# Revit family: IS_ConceptAir_Multiproduct_BIM_GB_E0848;E0849;E0851;E0852
name_source: partatom
category: Plumbing Fixtures
revit_build: Autodesk Revit MEP 2014 (Build: 20140709_2115(x64)
units: mm (PartAtom-declared; Revit-internal decimal feet)

## types (24) — shared parameters
Accessories = www.idealspec.co.uk
AreaUnits = millimeters
Assembly Code = C1030200
AssetType = Fixed
BREEAM = No
Brand = Ideal Standard
Default Elevation = 800 mm  [stored 2.62467 ft]
DurationUnit = year
ECA = No
ExpectedLife = 10
Finish = White
IfcExportAs = IfcFurnitureType
IfcExportType = USERDEFINED
InstallationInstructions = www.idealspec.co.uk/resources.html
LinearUnits = millimeters
MainColor = White
ManufacturerURL = www.idealspec.co.uk
Material = Laquered MDF
NBSDescription = Bathroom integrated duct work
NBSReference = 45-35-72/320
NettWeight = 0 Kg
NominalDepth = 440 mm  [stored 1.44357 ft]
NominalHeight = 18 mm  [stored 0.0590551 ft]
NominalLength = 440 mm  [stored 1.44357 ft]
Shape = Rectangular
Space = Internal
SpareParts = www.fastpart-spares.co.uk
TMV3 = No
URL = www.idealspec.co.uk
Uniclass2 = Pr_40_30_78_04
Version = 1
VolumeUnits = Litres
WRAS = No
WarrantyDescription = Manufacturers warranty
WarrantyDurationParts = 5
WarrantyDurationUnit = year
WaterEfficientProduct = No
zero-valued in all types: CWFU, Cost, HWFU, WFU

## per-type parameters (varying)
| type | BIMObjectName | Color | Description | Features | MainColour | Model | ModelNumber | ModelReference | Name | NominalWidth | ProductInformation | Size |
| E0852VY - 120CM Worktop for Vessel Installation Matt Dark Brown | ISI_IdealStandard_Furniture_ConceptAir_E0852VY | Dark brown | Concept Air 120 cm Worktop For Vessel Installation Matt Dark Brown | 120 cm Worktop For Vessel Installation Matt Dark Brown | ISI_IdealStandard_Furniture_DarkBrown_Render | E0852VY | E0852VY | 120CM Worktop for Vessel Installation Gls Dark Brown + Matt White | Furniture_ConceptAir_E0852VY_IdealStandard | 1200 mm | www.idealspec.co.uk/assets/datasheet/E0852VY | 442 x 18 x 1204 mm |
| E0852UK - 120CM Worktop for Vessel Installation Wood Light Brown | ISI_IdealStandard_Furniture_ConceptAir_E0852UK | Wood brown | Concept Air 120 cm Worktop For Vessel Installation Wood Light Brown | 120 cm Worktop For Vessel Installation Wood Light Brown | ISI_IdealStandard_Furniture_WoodLightBrown_Render | E0852UK | E0852UK | 120CM Worktop for Vessel Installation Wood Light Brown + Matt Light Brown | Furniture_ConceptAir_E0852UK_IdealStandard | 1200 mm | www.idealspec.co.uk/assets/datasheet/E0852UK | 442 x 18 x 1204 mm |
| E0852PS - 120CM Worktop for Vessel Installation Wood Light Grey | ISI_IdealStandard_Furniture_ConceptAir_E0852PS | Wood grey | Concept Air 120 cm Worktop For Vessel Installation Wood Light Grey | 120 cm Worktop For Vessel Installation Wood Light Grey | ISI_IdealStandard_Furniture_WoodLightGrey_Render | E0852PS | E0852PS | 120CM Worktop for Vessel Installation Wood Light Grey + Matt White | Furniture_ConceptAir_E0852PS_IdealStandard | 1200 mm | www.idealspec.co.uk/assets/datasheet/E0852PS | 442 x 18 x 1204 mm |
| E0852KN - 120CM Worktop for Vessel Installation Gls White | ISI_IdealStandard_Furniture_ConceptAir_E0852KN | White | Concept Air 120 cm Worktop For Vessel Installation Gls White | 120 cm Worktop For Vessel Installation Gls White | ISI_IdealStandard_Laminate_White_Render | E0852KN | E0852KN | 120CM Worktop for Vessel Installation Gls White + Matt Light Grey | Furniture_ConceptAir_E0852KN_IdealStandard | 1200 mm | www.idealspec.co.uk/assets/datasheet/E0852KN | 442 x 18 x 1204 mm |
| E0852EQ - 120CM Worktop for Vessel Installation Gls Light Grey | ISI_IdealStandard_Furniture_ConceptAir_E0852EQ | Grey | Concept Air 120 cm Worktop For Vessel Installation Gls Light Grey | 120 cm Worktop For Vessel Installation Gls Light Grey | ISI_IdealStandard_Furniture_Grey_Render | E0852EQ | E0852EQ | 120CM Worktop for Vessel Installation Gls Light Grey + Matt White | Furniture_ConceptAir_E0852EQ_IdealStandard | 1200 mm | www.idealspec.co.uk/assets/datasheet/E0852EQ | 442 x 18 x 1204 mm |
| E0852B2 - 120CM Worktop for Vessel Installation Gls White | ISI_IdealStandard_Furniture_ConceptAir_E0852B2 | White | Concept Air 120 cm Worktop For Vessel Installation Gls White | 120 cm Worktop For Vessel Installation Gls White | ISI_IdealStandard_Laminate_White_Render | E0852B2 | E0852B2 | 120CM Worktop for Vessel Installation Gls White + Matt White | Furniture_ConceptAir_E0852B2_IdealStandard | 1200 mm | www.idealspec.co.uk/assets/datasheet/E0852B2 | 442 x 18 x 1204 mm |
| E0851VY - 100CM Worktop for Vessel Installation Matt Dark Brown | ISI_IdealStandard_Furniture_ConceptAir_E0851VY | Dark brown | Concept Air 100 cm Worktop For Vessel Installation Matt Dark Brown | 100 cm Worktop For Vessel Installation Matt Dark Brown | ISI_IdealStandard_Furniture_DarkBrown_Render | E0851VY | E0851VY | 100CM Worktop for Vessel Installation Gls Dark Brown + Matt White | Furniture_ConceptAir_E0851VY_IdealStandard | 1000 mm  [stored 3.28084 ft] | www.idealspec.co.uk/assets/datasheet/E0851VY | 442 x 18 x 1004 mm |
| E0851UK - 100CM Worktop for Vessel Installation Wood Light Brown | ISI_IdealStandard_Furniture_ConceptAir_E0851UK | Wood brown | Concept Air 100 cm Worktop For Vessel Installation Wood Light Brown | 100 cm Worktop For Vessel Installation Wood Light Brown | ISI_IdealStandard_Furniture_WoodLightBrown_Render | E0851UK | E0851UK | 100CM Worktop for Vessel Installation Wood Light Brown + Matt Light Brown | Furniture_ConceptAir_E0851UK_IdealStandard | 1000 mm  [stored 3.28084 ft] | www.idealspec.co.uk/assets/datasheet/E0851UK | 442 x 18 x 1004 mm |
| E0851PS - 100CM Worktop for Vessel Installation Wood Light Grey | ISI_IdealStandard_Furniture_ConceptAir_E0851PS | Wood grey | Concept Air 100 cm Worktop For Vessel Installation Wood Light Grey | 100 cm Worktop For Vessel Installation Wood Light Grey | ISI_IdealStandard_Furniture_WoodLightGrey_Render | E0851PS | E0851PS | 100CM Worktop for Vessel Installation Wood Light Grey + Matt White | Furniture_ConceptAir_E0851PS_IdealStandard | 1000 mm  [stored 3.28084 ft] | www.idealspec.co.uk/assets/datasheet/E0851PS | 442 x 18 x 1004 mm |
| E0851KN - 100CM Worktop for Vessel Installation Gls White | ISI_IdealStandard_Furniture_ConceptAir_E0851KN | White | Concept Air 100 cm Worktop For Vessel Installation Gls White | 100 cm Worktop For Vessel Installation Gls White | ISI_IdealStandard_Laminate_White_Render | E0851KN | E0851KN | 100CM Worktop for Vessel Installation Gls White + Matt Light Grey | Furniture_ConceptAir_E0851KN_IdealStandard | 1000 mm  [stored 3.28084 ft] | www.idealspec.co.uk/assets/datasheet/E0851KN | 442 x 18 x 1004 mm |
| E0851EQ - 100CM Worktop for Vessel Installation Gls Light Grey | ISI_IdealStandard_Furniture_ConceptAir_E0851EQ | Grey | Concept Air 100 cm Worktop For Vessel Installation Gls Light Grey | 100 cm Worktop For Vessel Installation Gls Light Grey | ISI_IdealStandard_Furniture_Grey_Render | E0851EQ | E0851EQ | 100CM Worktop for Vessel Installation Gls Light Grey + Matt White | Furniture_ConceptAir_E0851EQ_IdealStandard | 1000 mm  [stored 3.28084 ft] | www.idealspec.co.uk/assets/datasheet/E0851EQ | 442 x 18 x 1004 mm |
| E0851B2 - 100CM Worktop for Vessel Installation Gls White | ISI_IdealStandard_Furniture_ConceptAir_E0851B2 | White | Concept Air 100 cm Worktop For Vessel Installation Gls White | 100 cm Worktop For Vessel Installation Gls White | ISI_IdealStandard_Laminate_White_Render | E0851B2 | E0851B2 | 100CM Worktop for Vessel Installation Gls White + Matt White | Furniture_ConceptAir_E0851B2_IdealStandard | 1000 mm  [stored 3.28084 ft] | www.idealspec.co.uk/assets/datasheet/E0851B2 | 442 x 18 x 1004 mm |
| E0849VY - 80CM Worktop for Vessel Installation Matt Dark Brown | ISI_IdealStandard_Furniture_ConceptAir_E0849VY | Dark brown | Concept Air 80 cm Worktop For Vessel Installation Matt Dark Brown | 80 cm Worktop For Vessel Installation Matt Dark Brown | ISI_IdealStandard_Furniture_DarkBrown_Render | E0849VY | E0849VY | 80CM Worktop for Vessel Installation Gls Dark Brown + Matt White | Furniture_ConceptAir_E0849VY_IdealStandard | 800 mm  [stored 2.62467 ft] | www.idealspec.co.uk/assets/datasheet/E0849VY | 442 x 18 x 804 mm |
| E0849UK - 80CM Worktop for Vessel Installation Wood Light Brown | ISI_IdealStandard_Furniture_ConceptAir_E0849UK | Wood brown | Concept Air 80 cm Worktop For Vessel Installation Wood Light Brown | 80 cm Worktop For Vessel Installation Wood Light Brown | ISI_IdealStandard_Furniture_WoodLightBrown_Render | E0849UK | E0849UK | 80CM Worktop for Vessel Installation Wood Light Brown + Matt Light Brown | Furniture_ConceptAir_E0849UK_IdealStandard | 800 mm  [stored 2.62467 ft] | www.idealspec.co.uk/assets/datasheet/E0849UK | 442 x 18 x 804 mm |
| E0849PS - 80CM Worktop for Vessel Installation Wood Light Grey | ISI_IdealStandard_Furniture_ConceptAir_E0849PS | Wood grey | Concept Air 80 cm Worktop For Vessel Installation Wood Light Grey | 80 cm Worktop For Vessel Installation Wood Light Grey | ISI_IdealStandard_Furniture_WoodLightGrey_Render | E0849PS | E0849PS | 80CM Worktop for Vessel Installation Wood Light Grey + Matt White | Furniture_ConceptAir_E0849PS_IdealStandard | 800 mm  [stored 2.62467 ft] | www.idealspec.co.uk/assets/datasheet/E0849PS | 442 x 18 x 804 mm |
| E0849KN - 80CM Worktop for Vessel Installation Gls White | ISI_IdealStandard_Furniture_ConceptAir_E0849KN | White | Concept Air 80 cm Worktop For Vessel Installation Gls White | 80 cm Worktop For Vessel Installation Gls White | ISI_IdealStandard_Laminate_White_Render | E0849KN | E0849KN | 80CM Worktop for Vessel Installation Gls White + Matt Light Grey | Furniture_ConceptAir_E0849KN_IdealStandard | 800 mm  [stored 2.62467 ft] | www.idealspec.co.uk/assets/datasheet/E0849KN | 442 x 18 x 804 mm |
| E0849EQ - 80CM Worktop for Vessel Installation Gls Light Grey | ISI_IdealStandard_Furniture_ConceptAir_E0849EQ | Grey | Concept Air 80 cm Worktop For Vessel Installation Gls Light Grey | 80 cm Worktop For Vessel Installation Gls Light Grey | ISI_IdealStandard_Furniture_Grey_Render | E0849EQ | E0849EQ | 80CM Worktop for Vessel Installation Gls Light Grey + Matt White | Furniture_ConceptAir_E0849EQ_IdealStandard | 800 mm  [stored 2.62467 ft] | www.idealspec.co.uk/assets/datasheet/E0849EQ | 442 x 18 x 804 mm |
| E0849B2 - 80CM Worktop for Vessel Installation Gls White | ISI_IdealStandard_Furniture_ConceptAir_E0849B2 | White | Concept Air 80 cm Worktop For Vessel Installation Gls White | 80 cm Worktop For Vessel Installation Gls White | ISI_IdealStandard_Laminate_White_Render | E0849B2 | E0849B2 | 80CM Worktop for Vessel Installation Gls White + Matt White | Furniture_ConceptAir_E0849B2_IdealStandard | 800 mm  [stored 2.62467 ft] | www.idealspec.co.uk/assets/datasheet/E0849B2 | 442 x 18 x 804 mm |
| E0848VY - 60CM Worktop for Vessel Installation Matt Dark Brown | ISI_IdealStandard_Furniture_ConceptAir_E0848VY | Dark brown | Concept Air 60 cm Worktop For Vessel Installation Matt Dark Brown | 60 cm Worktop For Vessel Installation Matt Dark Brown | ISI_IdealStandard_Furniture_DarkBrown_Render | E0848VY | E0848VY | 60CM Worktop for Vessel Installation Gls Dark Brown + Matt White | Furniture_ConceptAir_E0848VY_IdealStandard | 600 mm | www.idealspec.co.uk/assets/datasheet/E0848VY | 442 x 18 x 604 mm |
| E0848UK - 60CM Worktop for Vessel Installation Wood Light Brown | ISI_IdealStandard_Furniture_ConceptAir_E0848UK | Wood brown | Concept Air 60 cm Worktop For Vessel Installation Wood Light Brown | 60 cm Worktop For Vessel Installation Wood Light Brown | ISI_IdealStandard_Furniture_WoodLightBrown_Render | E0848UK | E0848UK | 60CM Worktop for Vessel Installation Wood Light Brown + Matt Light Brown | Furniture_ConceptAir_E0848UK_IdealStandard | 600 mm | www.idealspec.co.uk/assets/datasheet/E0848UK | 442 x 18 x 604 mm |
| E0848PS - 60CM Worktop for Vessel Installation Wood Light Grey | ISI_IdealStandard_Furniture_ConceptAir_E0848PS | Wood grey | Concept Air 60 cm Worktop For Vessel Installation Wood Light Grey | 60 cm Worktop For Vessel Installation Wood Light Grey | ISI_IdealStandard_Furniture_WoodLightGrey_Render | E0848PS | E0848PS | 60CM Worktop for Vessel Installation Wood Light Grey + Matt White | Furniture_ConceptAir_E0848PS_IdealStandard | 600 mm | www.idealspec.co.uk/assets/datasheet/E0848PS | 442 x 18 x 604 mm |
| E0848KN - 60CM Worktop for Vessel Installation Gls White | ISI_IdealStandard_Furniture_ConceptAir_E0848KN | White | Concept Air 60 cm Worktop For Vessel Installation Gls White | 60 cm Worktop For Vessel Installation Gls White | ISI_IdealStandard_Laminate_White_Render | E0848KN | E0848KN | 60CM Worktop for Vessel Installation Gls White + Matt Light Grey | Furniture_ConceptAir_E0848KN_IdealStandard | 600 mm | www.idealspec.co.uk/assets/datasheet/E0848KN | 442 x 18 x 604 mm |
| E0848EQ - 60CM Worktop for Vessel Installation Gls Light Grey | ISI_IdealStandard_Furniture_ConceptAir_E0848EQ | Grey | Concept Air 60 cm Worktop For Vessel Installation Gls Light Grey | 60 cm Worktop For Vessel Installation Gls Light Grey | ISI_IdealStandard_Furniture_Grey_Render | E0848EQ | E0848EQ | 60CM Worktop for Vessel Installation Gls Light Grey + Matt White | Furniture_ConceptAir_E0848EQ_IdealStandard | 600 mm | www.idealspec.co.uk/assets/datasheet/E0848EQ | 442 x 18 x 604 mm |
| E0848B2 - 60CM Worktop for Vessel Installation Gls White | ISI_IdealStandard_Furniture_ConceptAir_E0848B2 | White | Concept Air 60 cm Worktop For Vessel Installation Gls White | 60 cm Worktop For Vessel Installation Gls White | ISI_IdealStandard_Laminate_White_Render | E0848B2 | E0848B2 | 60CM Worktop for Vessel Installation Gls White + Matt White | Furniture_ConceptAir_E0848B2_IdealStandard | 600 mm | www.idealspec.co.uk/assets/datasheet/E0848B2 | 442 x 18 x 604 mm |

note: [stored X ft] marks values corroborated as IEEE doubles in the binary element streams (Revit-internal decimal feet)

## geometry (parser evidence)
native form markers: Sweep x1
no freeform markers — native parametric forms only
